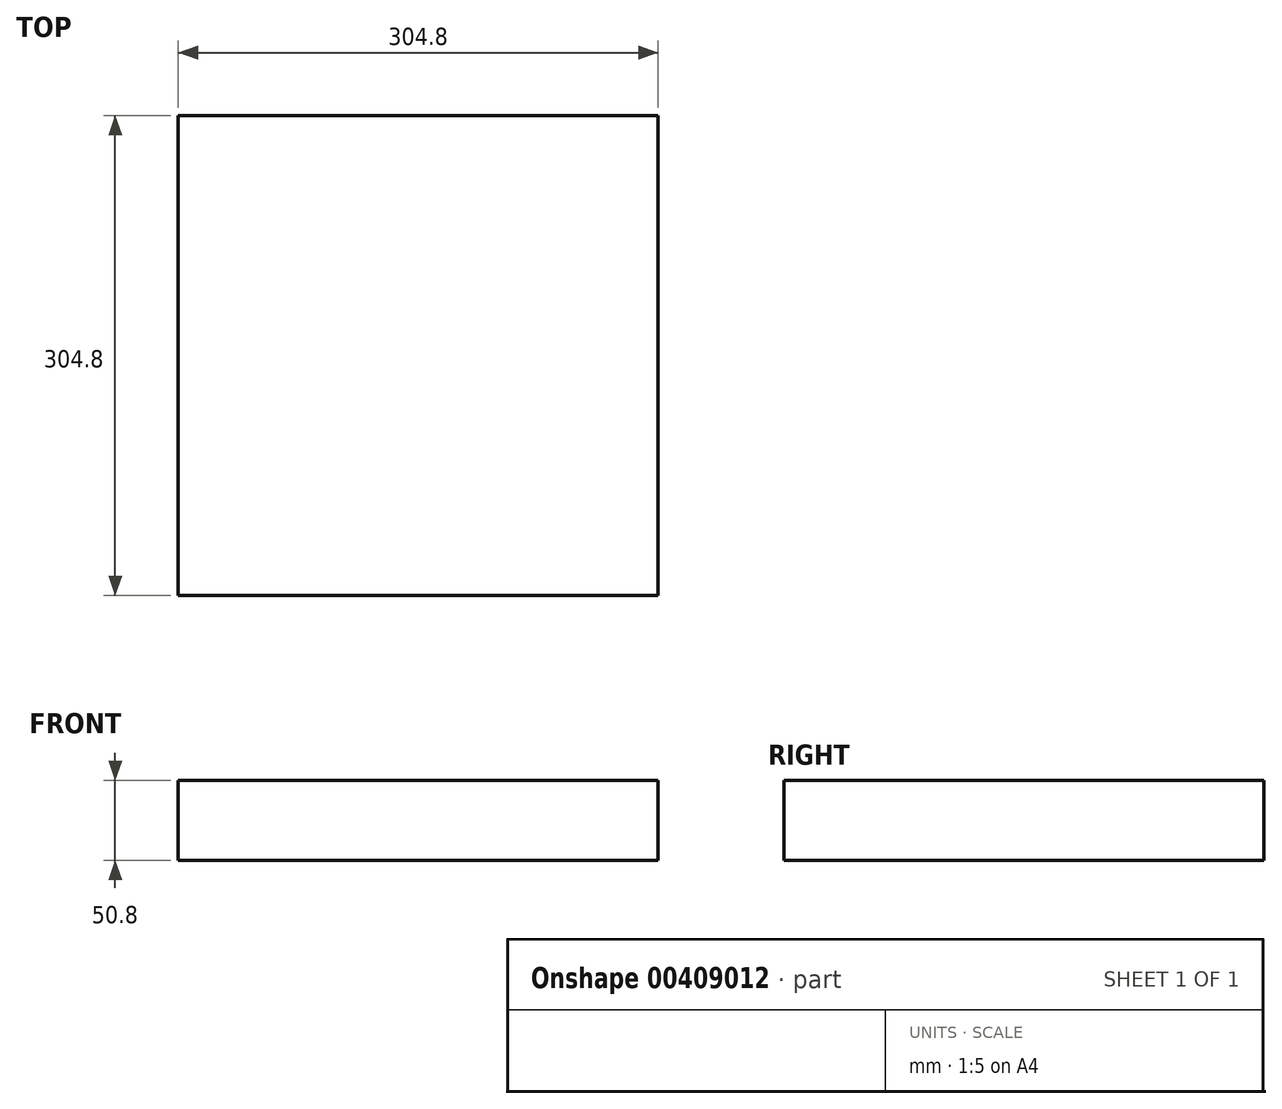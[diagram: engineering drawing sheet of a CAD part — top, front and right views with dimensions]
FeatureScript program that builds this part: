
annotation { "Feature Type Name" : "Feature", "Feature Type Description" : "" }
export const myFeature = defineFeature(function(context is Context, id is Id, definition is map)
    precondition{}
    {
        {
            var Q0;
            Q0=qCreatedBy(makeId("Top.planeOp"),FACE);
            var sketch = newSketch(context, id + "F0", { "sketchPlane" : qUnion([Q0])});
            skLineSegment(sketch, "E0.bottom", {"start": v(-144.68, 152.4) * mm, "end": v(160.12, 152.4) * mm});
            skLineSegment(sketch, "E0.top", {"start": v(-144.68, -152.4) * mm, "end": v(160.12, -152.4) * mm});
            skLineSegment(sketch, "E0.left", {"start": v(-144.68, 152.4) * mm, "end": v(-144.68, -152.4) * mm});
            skLineSegment(sketch, "E0.right", {"start": v(160.12, 152.4) * mm, "end": v(160.12, -152.4) * mm});
            skPoint(sketch, "E0.middle", {"position": v(7.72, 0) * mm});
            skSolve(sketch);
        }
        {
            var Q0;
            Q0=makeQuery(id+"F0.imprint","IMPRINT",FACE,{"disambiguationData":[TD([[makeQuery(id+"F0.imprint","IMPRINT",EDGE,{"derivedFrom":sQuery(id+"F0.wireOp",EDGE,"E0.bottom")}),-1.0]])]});
            extrude(context, id + "F1", {"entities" : qUnion([Q0]), "depth" : 50.8 * mm});
        }
    });
